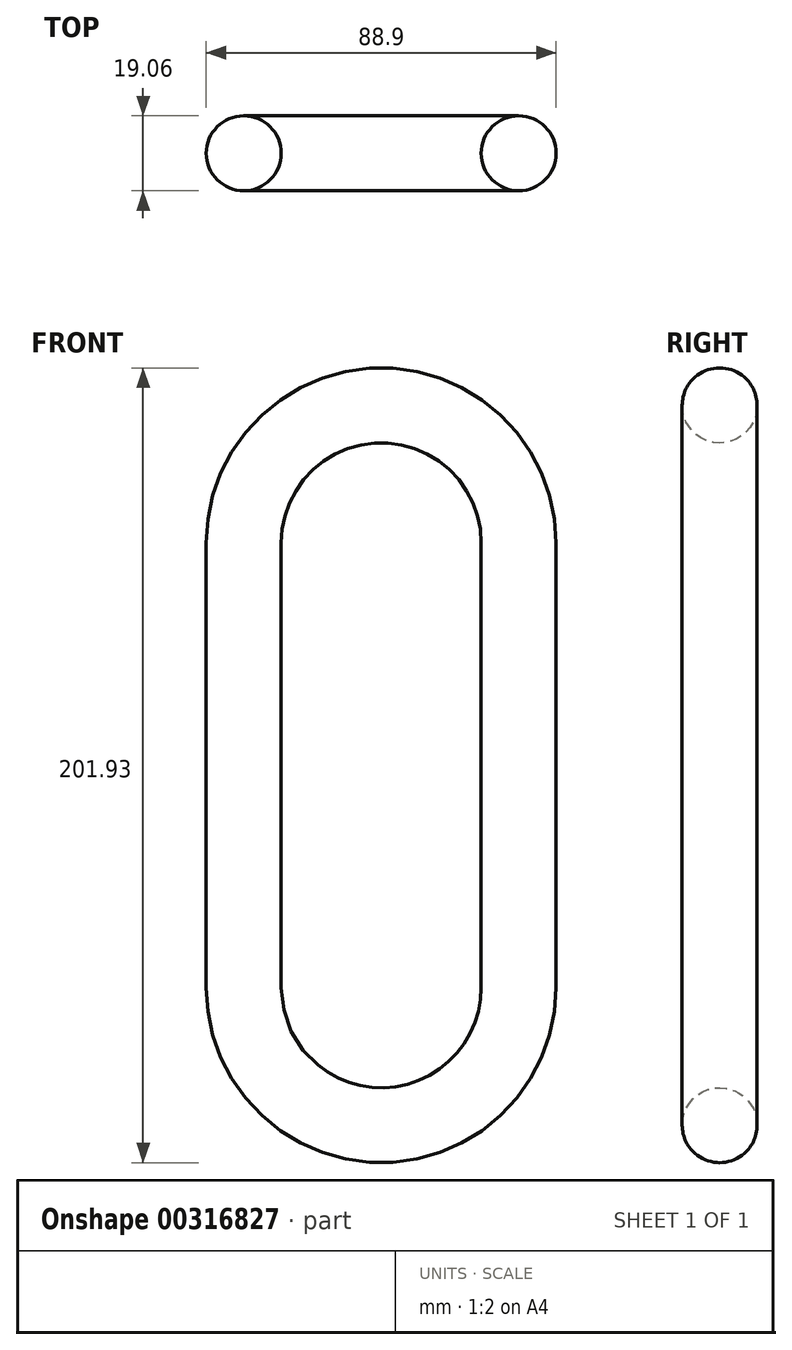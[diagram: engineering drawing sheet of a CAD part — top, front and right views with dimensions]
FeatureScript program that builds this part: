
annotation { "Feature Type Name" : "Feature", "Feature Type Description" : "" }
export const myFeature = defineFeature(function(context is Context, id is Id, definition is map)
    precondition{}
    {
        {
            var Q0;
            Q0=qCreatedBy(makeId("Front.planeOp"),FACE);
            var sketch = newSketch(context, id + "F0", { "sketchPlane" : qUnion([Q0])});
            skLineSegment(sketch, "E0", {"start": v(-25.4, 0) * mm, "end": v(-25.4, -35.69) * mm});
            skLineSegment(sketch, "E1.MirrorCS", {"start": v(25.4, 0) * mm, "end": v(25.4, -35.69) * mm});
            skArc(sketch, "E2", {"start": v(-25.4, -35.69) * mm, "mid": v(0, -61.09) * mm, "end": v(25.4, -35.69) * mm});
            skLineSegment(sketch, "E3", {"start": v(-25.4, 0) * mm, "end": v(-25.4, 77.34) * mm});
            skLineSegment(sketch, "E4", {"start": v(25.4, 0) * mm, "end": v(25.4, 77.34) * mm});
            skArc(sketch, "E5", {"start": v(25.4, 77.34) * mm, "mid": v(0, 102.74) * mm, "end": v(-25.4, 77.34) * mm});
            skLineSegment(sketch, "E6", {"start": v(0, 102.74) * mm, "end": v(0, -80.14) * mm, "construction": true});
            skSolve(sketch);
        }
        {
            var Q0;
            Q0=qCreatedBy(makeId("Top.planeOp"),FACE);
            var sketch = newSketch(context, id + "F1", { "sketchPlane" : qUnion([Q0])});
            skPoint(sketch, "E7.0", {"position": v(25.4, 0) * mm});
            skCircle(sketch, "E8", {"center": v(34.92, 0) * mm, "radius": 9.53 * mm});
            skSolve(sketch);
        }
        {
            var Q0;
            Q0=makeQuery(id+"F1.imprint","IMPRINT",FACE,{"disambiguationData":[TD([[makeQuery(id+"F1.imprint","IMPRINT",EDGE,{"derivedFrom":sQuery(id+"F1.wireOp",EDGE,"E8")}),1.0]])]});
            var Q1;
            Q1=sQuery(id+"F0.wireOp",EDGE,"E4");
            var Q2;
            Q2=sQuery(id+"F0.wireOp",EDGE,"E5");
            var Q3;
            Q3=sQuery(id+"F0.wireOp",EDGE,"E3");
            var Q4;
            Q4=sQuery(id+"F0.wireOp",EDGE,"E0");
            var Q5;
            Q5=sQuery(id+"F0.wireOp",EDGE,"E2");
            var Q6;
            Q6=sQuery(id+"F0.wireOp",EDGE,"E1.MirrorCS");
            sweep(context, id + "F2", {"profiles" : qUnion([Q0]), "path" : qUnion([Q1, Q2, Q3, Q4, Q5, Q6])});
        }
    });
